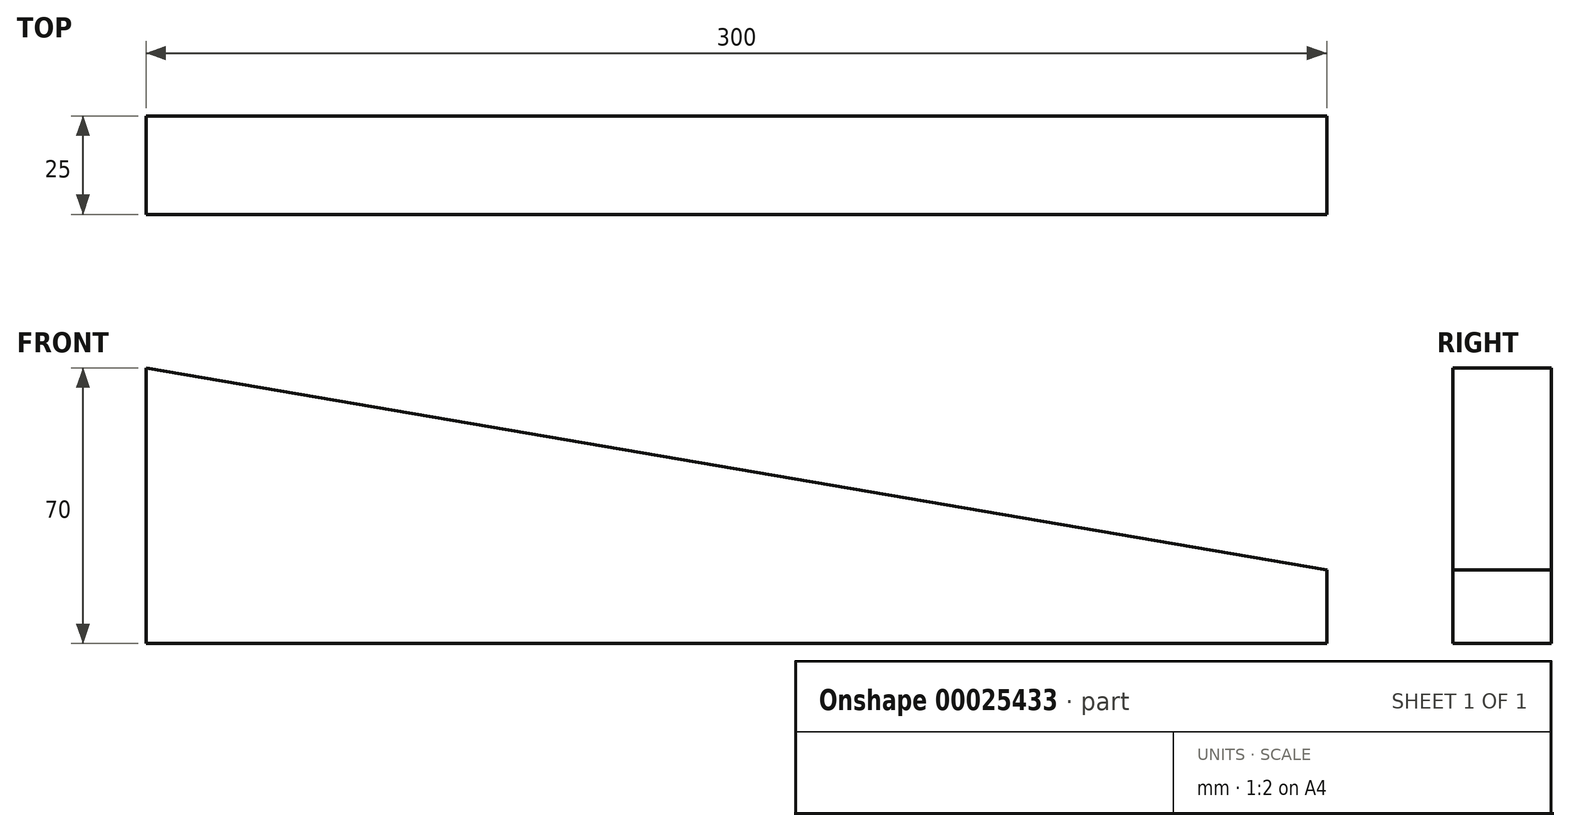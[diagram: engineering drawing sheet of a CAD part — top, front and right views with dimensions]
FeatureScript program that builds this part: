
annotation { "Feature Type Name" : "Feature", "Feature Type Description" : "" }
export const myFeature = defineFeature(function(context is Context, id is Id, definition is map)
    precondition{}
    {
        {
            var Q0;
            Q0=qCreatedBy(makeId("Front.planeOp"),FACE);
            var sketch = newSketch(context, id + "F0", { "sketchPlane" : qUnion([Q0])});
            skLineSegment(sketch, "E0", {"start": v(-142.93, 41.58) * mm, "end": v(-142.93, -28.42) * mm});
            skLineSegment(sketch, "E1", {"start": v(-142.93, -28.42) * mm, "end": v(157.07, -28.42) * mm});
            skLineSegment(sketch, "E2", {"start": v(-142.93, 41.58) * mm, "end": v(157.07, -9.7) * mm});
            skLineSegment(sketch, "E3", {"start": v(157.07, -9.7) * mm, "end": v(157.07, -28.42) * mm});
            skSolve(sketch);
        }
        {
            var Q0;
            Q0 = qSketchRegion(id + "F0", true);
            extrude(context, id + "F1", {"entities" : qUnion([Q0]), "depth" : 25 * mm});
        }
    });
